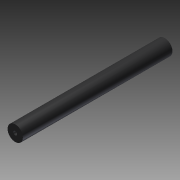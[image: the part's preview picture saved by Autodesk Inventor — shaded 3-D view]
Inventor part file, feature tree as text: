
AUTODESK INVENTOR PART (.ipt)
format: ipt  version: 2012 (Build 160160000, 160)  size: 70,144 bytes
history: native  units: in
note: dims shown in document units (in); Inventor stores cm internally (conversion verified against a paired STEP export)
features: extrude x1, sketch x1
ambient origin geometry x8: Origin, YZ Plane, XZ Plane, XY Plane, X Axis, Y Axis, Z Axis, Center Point
bodies: Solid1 (feature_tree)
feature tree (2):
  extrude  "Extrusion1"  Depth=2.0in
  sketch  "Sketch1"  dims[d0=0.5in d1=2.0in d2=19.5in d3=0.0in]
